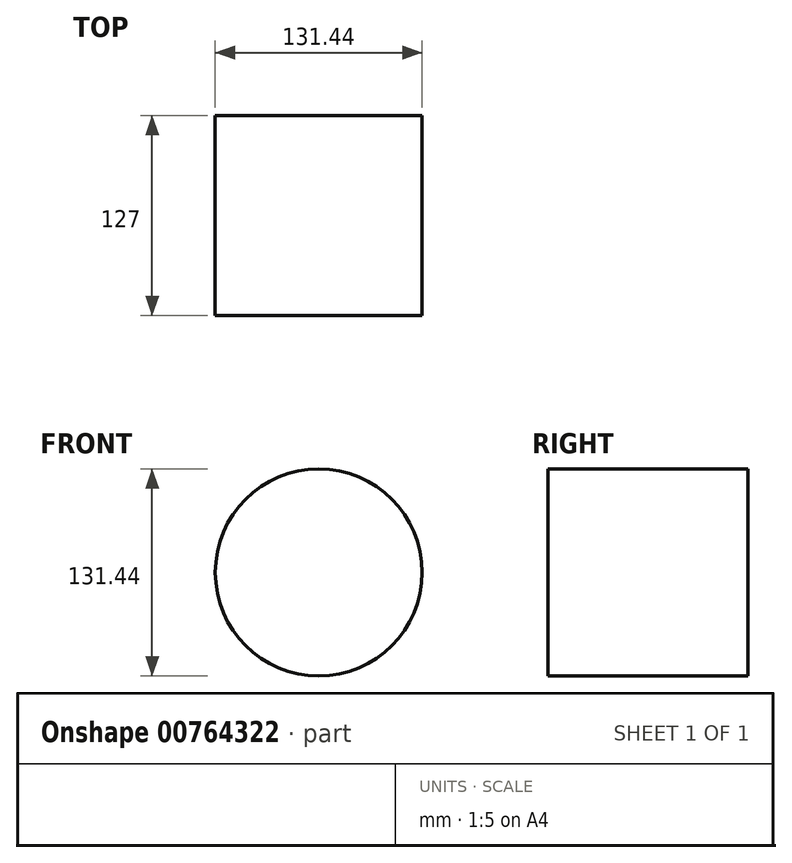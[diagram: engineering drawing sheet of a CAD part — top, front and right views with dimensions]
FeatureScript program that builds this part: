
annotation { "Feature Type Name" : "Feature", "Feature Type Description" : "" }
export const myFeature = defineFeature(function(context is Context, id is Id, definition is map)
    precondition{}
    {
        {
            var Q0;
            Q0=qCreatedBy(makeId("Front.planeOp"),FACE);
            var sketch = newSketch(context, id + "F0", { "sketchPlane" : qUnion([Q0])});
            skCircle(sketch, "E0", {"center": v(0, 0) * mm, "radius": 65.72 * mm});
            skSolve(sketch);
        }
        {
            var Q0;
            Q0=makeQuery(id+"F0.imprint","IMPRINT",FACE,{"disambiguationData":[TD([[makeQuery(id+"F0.imprint","IMPRINT",EDGE,{"derivedFrom":sQuery(id+"F0.wireOp",EDGE,"E0")}),1.0]])]});
            extrude(context, id + "F1", {"entities" : qUnion([Q0]), "depth" : 127 * mm, "offsetDistance" : 25 * mm});
        }
    });
